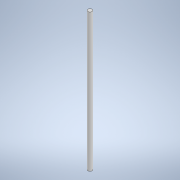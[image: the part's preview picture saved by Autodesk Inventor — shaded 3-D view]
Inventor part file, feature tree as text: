
AUTODESK INVENTOR PART (.ipt)
format: ipt  version: 2020.1 (Build 241239000, 239)  size: 90,112 bytes
history: native  units: mm
features: extrude x1, sketch x1
ambient origin geometry x8: Origin, YZ Plane, XZ Plane, XY Plane, X Axis, Y Axis, Z Axis, Center Point
bodies: Solid1 (feature_tree)
feature tree (2):
  extrude  "Extrusion1"  Depth=210.0mm TaperAngle=0.0deg
  sketch  "Sketch1"  dims[d0=6.35mm d1=210.0mm d2=0.0mm]
